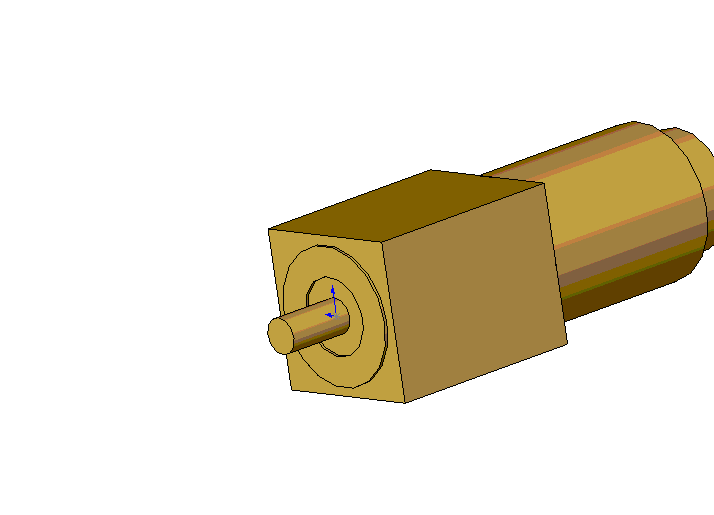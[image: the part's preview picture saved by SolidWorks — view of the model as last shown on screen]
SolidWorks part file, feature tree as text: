
SOLIDWORKS PART (.sldprt)
format: sldprt  version: not decoded by parser v0  size: 95,744 bytes
history: native  units: mm
features: sketch x6, extrude x6 (+10 scaffold rows collapsed)
feature tree (22):
  scaffold x10  (default folders/planes/origin — collapsed)
  sketch  "Sketch1"  dims[D1=82.55mm D2=82.55mm D3=82.55mm]
  extrude  "Extrude1"  Depth=111.125mm
  sketch  "Sketch2"
  extrude  "Extrude2"  Depth=103.1875mm
  sketch  "Sketch3"  dims[D1=63.5mm]
  extrude  "Extrude3"  Depth=23.8125mm
  sketch  "Sketch4"  dims[D1=6.35mm]
  extrude  "Extrude4"  Depth=22.225mm
  sketch  "Sketch5"  dims[D1=19.05mm]
  extrude  "Extrude5"  Depth=38.1mm
  sketch  "Sketch6"  dims[D1=73.025mm D2=41.275mm]
  extrude  "Extrude6"  Depth=1.5875mm
decode coverage: 11 of 12 modeling features carry decoded parameters
note: suppression state not decoded; provenance and decode notes live in map.json
